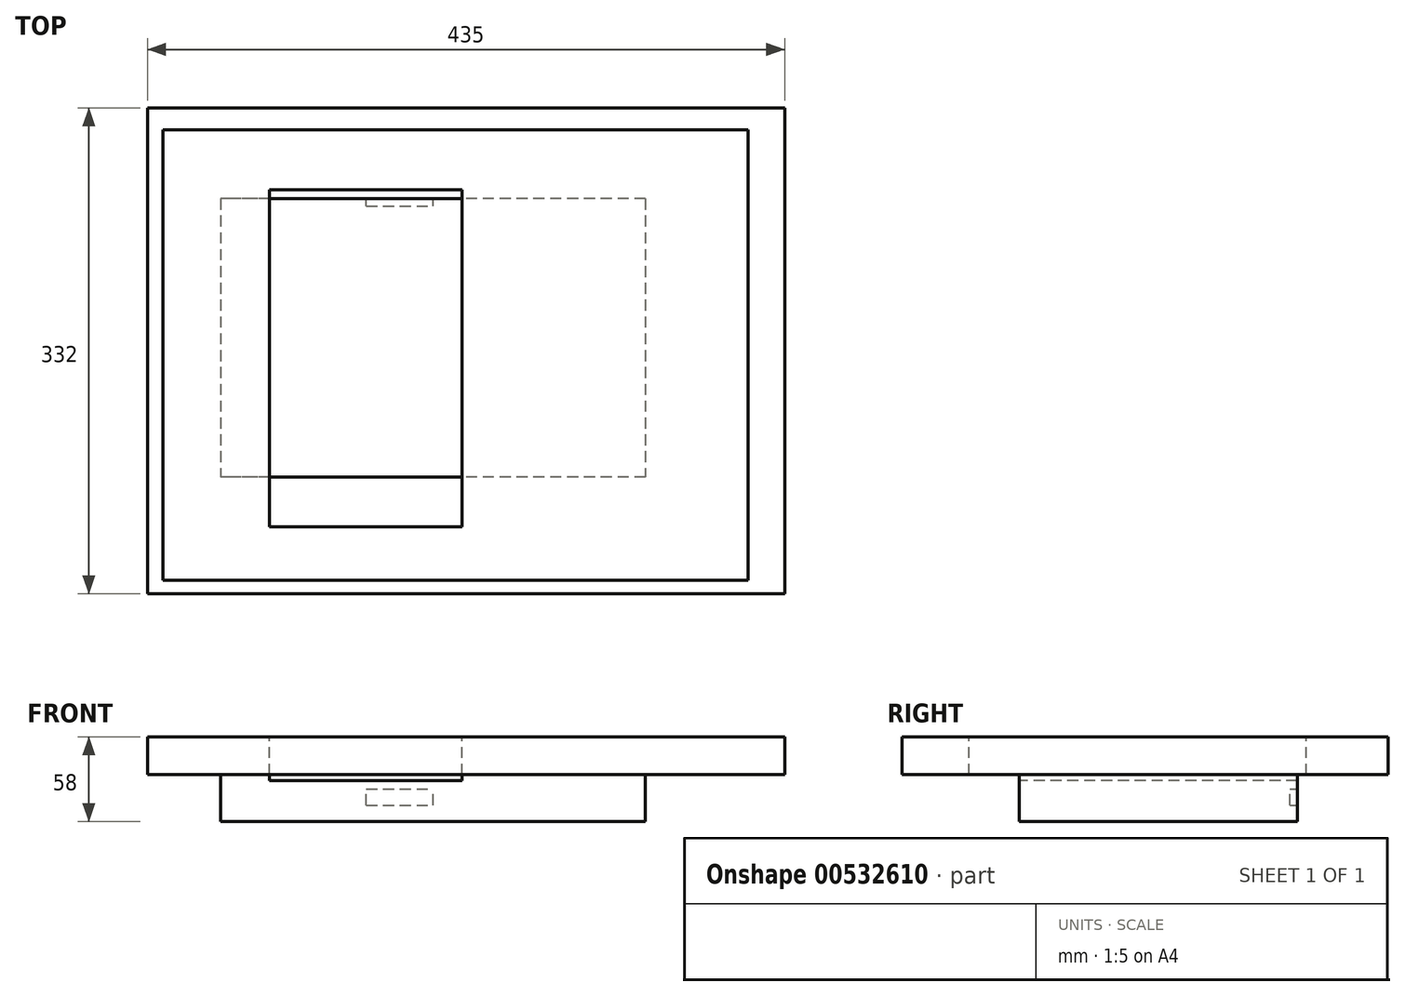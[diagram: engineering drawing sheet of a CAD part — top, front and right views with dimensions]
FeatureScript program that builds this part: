
annotation { "Feature Type Name" : "Feature", "Feature Type Description" : "" }
export const myFeature = defineFeature(function(context is Context, id is Id, definition is map)
    precondition{}
    {
        {
            var Q0;
            Q0=qCreatedBy(makeId("Top.planeOp"),FACE);
            var sketch = newSketch(context, id + "F0", { "sketchPlane" : qUnion([Q0])});
            skLineSegment(sketch, "E0.bottom", {"start": v(-217.5, -166) * mm, "end": v(217.5, -166) * mm});
            skLineSegment(sketch, "E0.top", {"start": v(-217.5, 166) * mm, "end": v(217.5, 166) * mm});
            skLineSegment(sketch, "E0.left", {"start": v(-217.5, -166) * mm, "end": v(-217.5, 166) * mm});
            skLineSegment(sketch, "E0.right", {"start": v(217.5, -166) * mm, "end": v(217.5, 166) * mm});
            skPoint(sketch, "E0.middle", {"position": v(0, 0) * mm});
            skSolve(sketch);
        }
        {
            var Q0;
            Q0=qSketchRegion(id+"F0",true);
            extrude(context, id + "F1", {"entities" : qUnion([Q0]), "depth" : 26 * mm});
        }
        {
            var Q0;
            Q0=makeQuery(id+"F1.opExtrude","CAP_FACE",FACE,{"disambiguationData":[OSD([sQuery(id+"F0.wireOp",EDGE,"E0.bottom"),sQuery(id+"F0.wireOp",EDGE,"E0.top"),sQuery(id+"F0.wireOp",EDGE,"E0.left"),sQuery(id+"F0.wireOp",EDGE,"E0.right")])],"isStart":false});
            var sketch = newSketch(context, id + "F2", { "sketchPlane" : qUnion([Q0])});
            skLineSegment(sketch, "E1.bottom", {"start": v(-206.9, 151) * mm, "end": v(192.5, 151) * mm});
            skLineSegment(sketch, "E1.top", {"start": v(-206.9, -156.5) * mm, "end": v(192.5, -156.5) * mm});
            skLineSegment(sketch, "E1.left", {"start": v(-206.9, 151) * mm, "end": v(-206.9, -156.5) * mm});
            skLineSegment(sketch, "E1.right", {"start": v(192.5, 151) * mm, "end": v(192.5, -156.5) * mm});
            skSolve(sketch);
        }
        {
            var Q0;
            Q0=makeQuery(id+"F2.imprint","IMPRINT",FACE,{"disambiguationData":[TD([[makeQuery(id+"F2.imprint","IMPRINT",EDGE,{"derivedFrom":sQuery(id+"F2.wireOp",EDGE,"E1.bottom")}),-1.0]])]});
            extrude(context, id + "F3", {"entities" : qUnion([Q0]), "operationType" : NewBodyOperationType.REMOVE, "oppositeDirection" : true, "depth" : 0.5 * mm});
        }
        {
            var Q0;
            Q0=makeQuery(id+"F0.imprint","IMPRINT",FACE,{"disambiguationData":[TD([[makeQuery(id+"F0.imprint","IMPRINT",EDGE,{"derivedFrom":sQuery(id+"F0.wireOp",EDGE,"E0.bottom")}),1.0]])]});
            var sketch = newSketch(context, id + "F4", { "sketchPlane" : qUnion([Q0])});
            skLineSegment(sketch, "E2.bottom", {"start": v(122.5, 104) * mm, "end": v(-167.5, 104) * mm});
            skLineSegment(sketch, "E2.top", {"start": v(122.5, -86) * mm, "end": v(-167.5, -86) * mm});
            skLineSegment(sketch, "E2.left", {"start": v(122.5, 104) * mm, "end": v(122.5, -86) * mm});
            skLineSegment(sketch, "E2.right", {"start": v(-167.5, 104) * mm, "end": v(-167.5, -86) * mm});
            skSolve(sketch);
        }
        {
            var Q0;
            Q0=qSketchRegion(id+"F4",true);
            extrude(context, id + "F5", {"entities" : qUnion([Q0]), "operationType" : NewBodyOperationType.ADD, "oppositeDirection" : true, "depth" : 32 * mm});
        }
        {
            var Q0;
            Q0=makeQuery(id+"F5.opExtrude","SWEPT_FACE",FACE,{"disambiguationData":[OSD([sQuery(id+"F4.wireOp",EDGE,"E2.bottom")])]});
            var sketch = newSketch(context, id + "F6", { "sketchPlane" : qUnion([Q0])});
            skPoint(sketch, "E3.oppositeSnap0", {"position": v(22.5, 0) * mm});
            skLineSegment(sketch, "E3.bottom", {"start": v(68.16, -20.72) * mm, "end": v(22.5, -20.72) * mm});
            skLineSegment(sketch, "E3.top", {"start": v(68.16, -9.84) * mm, "end": v(22.5, -9.84) * mm});
            skLineSegment(sketch, "E3.left", {"start": v(68.16, -20.72) * mm, "end": v(68.16, -9.84) * mm});
            skLineSegment(sketch, "E3.right", {"start": v(22.5, -20.72) * mm, "end": v(22.5, -9.84) * mm});
            skSolve(sketch);
        }
        {
            var Q0;
            Q0=qSketchRegion(id+"F6",true);
            extrude(context, id + "F7", {"entities" : qUnion([Q0]), "operationType" : NewBodyOperationType.REMOVE, "oppositeDirection" : true, "depth" : 5 * mm});
        }
        {
            var Q0;
            Q0=makeQuery(id+"F2.imprint","IMPRINT",FACE,{"disambiguationData":[TD([[makeQuery(id+"F2.imprint","IMPRINT",EDGE,{"derivedFrom":sQuery(id+"F2.wireOp",EDGE,"E1.bottom")}),-1.0]])]});
            var sketch = newSketch(context, id + "F8", { "sketchPlane" : qUnion([Q0])});
            skLineSegment(sketch, "E4.bottom", {"start": v(-134.01, 109.93) * mm, "end": v(-2.57, 109.93) * mm});
            skLineSegment(sketch, "E4.top", {"start": v(-134.01, -120.15) * mm, "end": v(-2.57, -120.15) * mm});
            skLineSegment(sketch, "E4.left", {"start": v(-134.01, 109.93) * mm, "end": v(-134.01, -120.15) * mm});
            skLineSegment(sketch, "E4.right", {"start": v(-2.57, 109.93) * mm, "end": v(-2.57, -120.15) * mm});
            skSolve(sketch);
        }
        {
            var Q0;
            Q0=makeQuery(id+"F8.imprint","IMPRINT",FACE,{"disambiguationData":[TD([[makeQuery(id+"F8.imprint","IMPRINT",EDGE,{"derivedFrom":sQuery(id+"F8.wireOp",EDGE,"E4.bottom")}),-1.0]])]});
            extrude(context, id + "F9", {"entities" : qUnion([Q0]), "operationType" : NewBodyOperationType.REMOVE, "oppositeDirection" : true, "depth" : 30 * mm, "offsetDistance" : 25 * mm});
        }
    });
